# Revit family: Sprinkler
name_source: partatom
category: Sprinklers
revit_build: Autodesk Revit MEP 2012 (Build: 20110309_2315(x64)
units: mm (PartAtom-declared; Revit-internal decimal feet)

## types (1)
- Sprinkler
    body end = -13 mm
    body start = 0 mm  [stored 0 ft]
    cap end = -6 mm  [stored -0.019685 ft]
    cap start = 0 mm  [stored 0 ft]
    npt end = 13 mm  [stored 0.0426509 ft]
    npt start = 0 mm  [stored 0 ft]
    pipe radius = 13 mm  [stored 0.0426509 ft]
    radius 2 = 19 mm
    reduser body end = 38 mm
    reduser top end = 41 mm
    reduser.5 end = 13 mm  [stored 0.0426509 ft]
    reduser.5 start = 10 mm  [stored 0.0328084 ft]
    reduserbody start = 13 mm  [stored 0.0426509 ft]
    redusertop start = 38 mm
    spout end = -51 mm
    spout start = -13 mm
    top end = -64 mm
    top start = -57 mm

note: [stored X ft] marks values corroborated as IEEE doubles in the binary element streams (Revit-internal decimal feet)

## geometry (parser evidence)
native form markers: Blend x4, Sweep x2
no freeform markers — native parametric forms only
